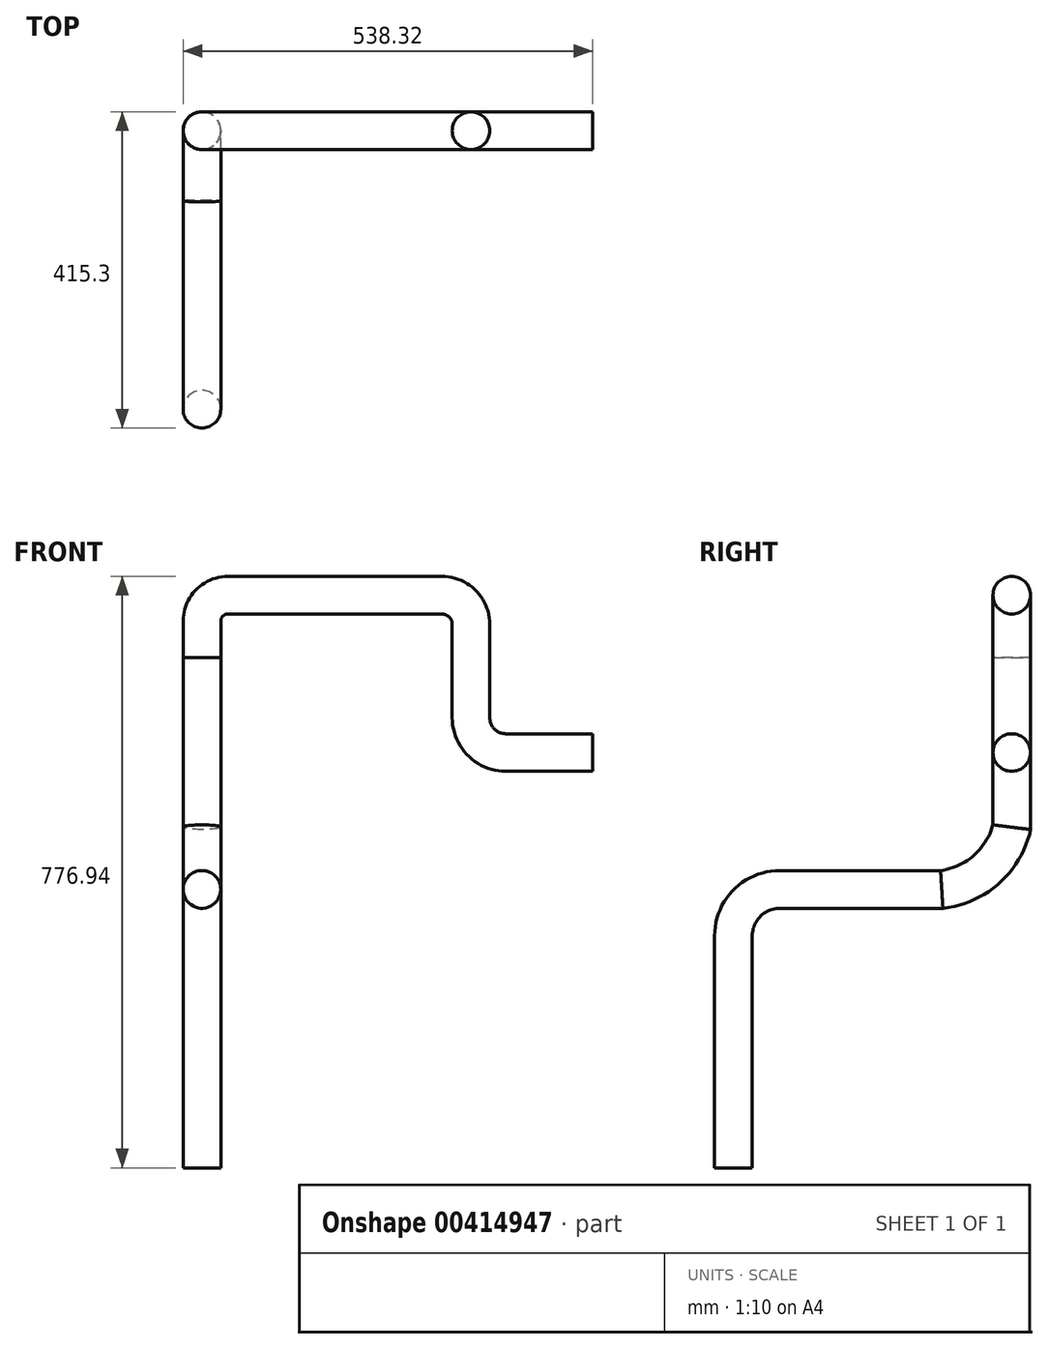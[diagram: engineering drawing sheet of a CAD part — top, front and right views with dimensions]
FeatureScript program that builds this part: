
annotation { "Feature Type Name" : "Feature", "Feature Type Description" : "" }
export const myFeature = defineFeature(function(context is Context, id is Id, definition is map)
    precondition{}
    {
        {
            var Q0;
            Q0=qCreatedBy(makeId("Right.planeOp"),FACE);
            var sketch = newSketch(context, id + "F0", { "sketchPlane" : qUnion([Q0])});
            skLineSegment(sketch, "E0", {"start": v(0, 0) * mm, "end": v(0, 304.8) * mm});
            skLineSegment(sketch, "E1", {"start": v(60.96, 365.76) * mm, "end": v(273.75, 365.76) * mm});
            skLineSegment(sketch, "E2", {"start": v(365.76, 447.45) * mm, "end": v(365.76, 670.56) * mm});
            skPoint(sketch, "E3.visualSharp", {"position": v(0, 365.76) * mm});
            skArc(sketch, "E3.filletArc", {"start": v(60.96, 365.76) * mm, "mid": v(17.85, 347.9) * mm, "end": v(0, 304.8) * mm});
            skArc(sketch, "E4", {"start": v(273.75, 365.76) * mm, "mid": v(332.5, 392.26) * mm, "end": v(365.76, 447.45) * mm});
            skSolve(sketch);
        }
        {
            var Q0;
            Q0=qCreatedBy(makeId("Top.planeOp"),FACE);
            var sketch = newSketch(context, id + "F1", { "sketchPlane" : qUnion([Q0])});
            skCircle(sketch, "E5", {"center": v(0, 0) * mm, "radius": 24.77 * mm});
            skSolve(sketch);
        }
        {
            var Q0;
            Q0=qCreatedBy(makeId("Front.planeOp"),FACE);
            cPlane(context, id + "F2", {"entities" : qUnion([Q0]), "cplaneType" : CPlaneType.OFFSET, "offset" : 365.76 * mm, "oppositeDirection" : true, "width" : 152.4 * mm, "height" : 152.4 * mm});
        }
        {
            var Q0;
            Q0=qCreatedBy(id+"F2.planeOp",FACE);
            var sketch = newSketch(context, id + "F3", { "sketchPlane" : qUnion([Q0])});
            skPoint(sketch, "E6.0", {"position": v(0, 670.56) * mm});
            skLineSegment(sketch, "E7", {"start": v(34.03, 752.25) * mm, "end": v(315.3, 752.25) * mm});
            skLineSegment(sketch, "E8", {"start": v(353.5, 714.04) * mm, "end": v(353.5, 591.32) * mm});
            skLineSegment(sketch, "E9", {"start": v(399.22, 545.6) * mm, "end": v(513.55, 545.6) * mm});
            skArc(sketch, "E10", {"start": v(353.5, 591.32) * mm, "mid": v(366.9, 558.99) * mm, "end": v(399.22, 545.6) * mm});
            skLineSegment(sketch, "E11.0", {"start": v(0, 670.56) * mm, "end": v(0, 718.22) * mm});
            skArc(sketch, "E12", {"start": v(34.03, 752.25) * mm, "mid": v(9.97, 742.28) * mm, "end": v(0, 718.22) * mm});
            skArc(sketch, "E13", {"start": v(353.5, 714.04) * mm, "mid": v(342.3, 741.06) * mm, "end": v(315.3, 752.25) * mm});
            skPoint(sketch, "E14.orphan", {"position": v(0, 447.45) * mm});
            skSolve(sketch);
        }
        {
            var Q0;
            Q0=makeQuery(id+"F1.imprint","IMPRINT",FACE,{"disambiguationData":[TD([[makeQuery(id+"F1.imprint","IMPRINT",EDGE,{"derivedFrom":sQuery(id+"F1.wireOp",EDGE,"E5")}),1.0]])]});
            var Q1;
            Q1=sQuery(id+"F0.wireOp",EDGE,"E0");
            var Q2;
            Q2=sQuery(id+"F0.wireOp",EDGE,"E3.filletArc");
            var Q3;
            Q3=sQuery(id+"F0.wireOp",EDGE,"E1");
            var Q4;
            Q4=sQuery(id+"F0.wireOp",EDGE,"E4");
            var Q5;
            Q5=sQuery(id+"F0.wireOp",EDGE,"E2");
            sweep(context, id + "F4", {"profiles" : qUnion([Q0]), "path" : qUnion([Q1, Q2, Q3, Q4, Q5])});
        }
        {
            var Q0;
            Q0=sQuery(id+"F3.wireOp",VERTEX,"E9.end");
            var Q1;
            Q1=qCreatedBy(makeId("Right.planeOp"),FACE);
            cPlane(context, id + "F5", {"entities" : qUnion([Q0, Q1]), "cplaneType" : CPlaneType.PLANE_POINT, "offset" : 25.4 * mm, "width" : 152.4 * mm, "height" : 152.4 * mm});
        }
        {
            var Q0;
            Q0=qCreatedBy(id+"F5.planeOp",FACE);
            var sketch = newSketch(context, id + "F6", { "sketchPlane" : qUnion([Q0])});
            skPoint(sketch, "E15.0", {"position": v(365.76, 545.6) * mm});
            skCircle(sketch, "E16", {"center": v(365.76, 545.6) * mm, "radius": 24.69 * mm});
            skSolve(sketch);
        }
        {
            var Q0;
            Q0=makeQuery(id+"F6.imprint","IMPRINT",FACE,{"disambiguationData":[TD([[makeQuery(id+"F6.imprint","IMPRINT",EDGE,{"derivedFrom":sQuery(id+"F6.wireOp",EDGE,"E16")}),1.0]])]});
            var Q1;
            Q1=sQuery(id+"F3.wireOp",EDGE,"E9");
            var Q2;
            Q2=sQuery(id+"F3.wireOp",EDGE,"E10");
            var Q3;
            Q3=sQuery(id+"F3.wireOp",EDGE,"E8");
            var Q4;
            Q4=sQuery(id+"F3.wireOp",EDGE,"E13");
            var Q5;
            Q5=sQuery(id+"F3.wireOp",EDGE,"E7");
            var Q6;
            Q6=sQuery(id+"F3.wireOp",EDGE,"E12");
            var Q7;
            Q7=sQuery(id+"F3.wireOp",EDGE,"E11.0");
            sweep(context, id + "F7", {"profiles" : qUnion([Q0]), "path" : qUnion([Q1, Q2, Q3, Q4, Q5, Q6, Q7])});
        }
    });
